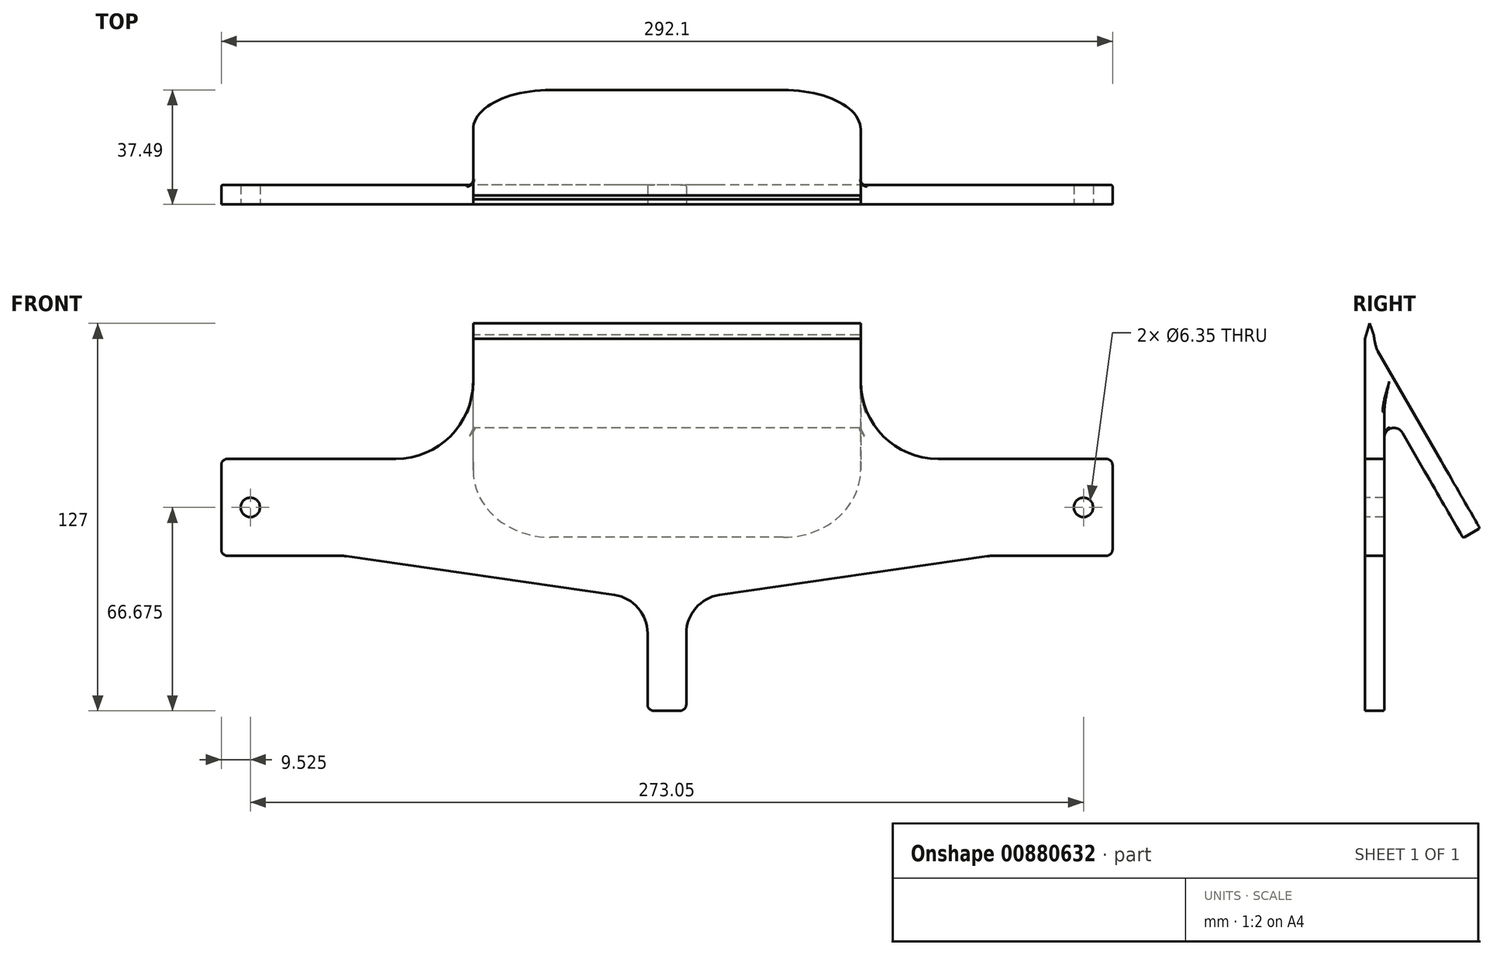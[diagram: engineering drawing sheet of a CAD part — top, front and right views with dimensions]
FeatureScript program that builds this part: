
annotation { "Feature Type Name" : "Feature", "Feature Type Description" : "" }
export const myFeature = defineFeature(function(context is Context, id is Id, definition is map)
    precondition{}
    {
        {
            var Q0;
            Q0=qCreatedBy(makeId("Right.planeOp"),FACE);
            var sketch = newSketch(context, id + "F0", { "sketchPlane" : qUnion([Q0])});
            skLineSegment(sketch, "E0", {"start": v(4.75, -127) * mm, "end": v(-1.6, -127) * mm});
            skLineSegment(sketch, "E1", {"start": v(-1.6, -127) * mm, "end": v(-1.6, -5.08) * mm});
            skPoint(sketch, "E2.orphan", {"position": v(-1.6, 0) * mm});
            skPoint(sketch, "E3.orphan", {"position": v(1.6, 0) * mm});
            skArc(sketch, "E4", {"start": v(1.27, -3.8) * mm, "mid": v(1.68, -6.21) * mm, "end": v(2.33, -8.56) * mm});
            skPoint(sketch, "E5.orphan", {"position": v(5.41, -5.08) * mm});
            skLineSegment(sketch, "E6", {"start": v(2.6, -9.17) * mm, "end": v(36.08, -67.16) * mm});
            skLineSegment(sketch, "E7", {"start": v(36.08, -67.16) * mm, "end": v(30.58, -70.33) * mm});
            skLineSegment(sketch, "E8", {"start": v(30.58, -70.33) * mm, "end": v(10.67, -35.86) * mm});
            skLineSegment(sketch, "E9", {"start": v(4.75, -127) * mm, "end": v(4.75, -37.45) * mm});
            skPoint(sketch, "E10.visualSharp", {"position": v(4.75, -25.6) * mm});
            skArc(sketch, "E10.filletArc", {"start": v(10.67, -35.86) * mm, "mid": v(7.1, -34.38) * mm, "end": v(4.75, -37.45) * mm});
            skPoint(sketch, "E11.visualSharp", {"position": v(2.44, -8.89) * mm});
            skArc(sketch, "E11.filletArc", {"start": v(2.33, -8.56) * mm, "mid": v(2.45, -8.87) * mm, "end": v(2.6, -9.17) * mm});
            skLineSegment(sketch, "E12", {"start": v(0, 0) * mm, "end": v(1.27, -3.8) * mm});
            skLineSegment(sketch, "E13", {"start": v(0, 0) * mm, "end": v(-1.6, -5.08) * mm});
            skSolve(sketch);
        }
        {
            var Q0;
            Q0=qSketchRegion(id+"F0",true);
            extrude(context, id + "F1", {"entities" : qUnion([Q0]), "endBound" : BoundingType.SYMMETRIC, "offsetDistance" : 25.4 * mm, "depth" : 292.1 * mm});
        }
        {
            var Q0;
            Q0=makeQuery(id+"F1.opExtrude","SWEPT_FACE",FACE,{"disambiguationData":[OSD([sQuery(id+"F0.wireOp",EDGE,"E1")])]});
            var sketch = newSketch(context, id + "F2", { "sketchPlane" : qUnion([Q0])});
            skLineSegment(sketch, "E14", {"start": v(-63.5, 0) * mm, "end": v(-63.5, -19.05) * mm});
            skLineSegment(sketch, "E15", {"start": v(-88.9, -44.45) * mm, "end": v(-144.02, -44.45) * mm});
            skLineSegment(sketch, "E16", {"start": v(-146.05, -46.48) * mm, "end": v(-146.05, -74.17) * mm});
            skLineSegment(sketch, "E17", {"start": v(-144.02, -76.2) * mm, "end": v(-106.83, -76.2) * mm});
            skLineSegment(sketch, "E18", {"start": v(-6.35, -101.6) * mm, "end": v(-6.35, -124.97) * mm});
            skLineSegment(sketch, "E19", {"start": v(-4.32, -127) * mm, "end": v(4.32, -127) * mm});
            skLineSegment(sketch, "E20", {"start": v(6.35, -124.97) * mm, "end": v(6.35, -101.6) * mm});
            skLineSegment(sketch, "E21", {"start": v(106.83, -76.2) * mm, "end": v(144.02, -76.2) * mm});
            skLineSegment(sketch, "E22", {"start": v(146.05, -74.17) * mm, "end": v(146.05, -46.48) * mm});
            skLineSegment(sketch, "E23", {"start": v(144.02, -44.45) * mm, "end": v(88.9, -44.45) * mm});
            skLineSegment(sketch, "E24", {"start": v(63.5, -19.05) * mm, "end": v(63.5, 0) * mm});
            skLineSegment(sketch, "E25", {"start": v(63.5, 0) * mm, "end": v(-63.5, 0) * mm});
            skLineSegment(sketch, "E26", {"start": v(0, 0) * mm, "end": v(0, -127) * mm, "construction": true});
            skPoint(sketch, "E27.visualSharp", {"position": v(-6.35, -76.2) * mm});
            skPoint(sketch, "E28.visualSharp", {"position": v(6.35, -76.2) * mm});
            skPoint(sketch, "E29.visualSharp", {"position": v(-63.5, -44.45) * mm});
            skArc(sketch, "E29.filletArc", {"start": v(-88.9, -44.45) * mm, "mid": v(-70.94, -37.01) * mm, "end": v(-63.5, -19.05) * mm});
            skPoint(sketch, "E30.visualSharp", {"position": v(6.35, -127) * mm});
            skArc(sketch, "E30.filletArc", {"start": v(4.32, -127) * mm, "mid": v(5.75, -126.4) * mm, "end": v(6.35, -124.97) * mm});
            skPoint(sketch, "E31.visualSharp", {"position": v(-6.35, -127) * mm});
            skArc(sketch, "E31.filletArc", {"start": v(-6.35, -124.97) * mm, "mid": v(-5.75, -126.4) * mm, "end": v(-4.32, -127) * mm});
            skPoint(sketch, "E32.visualSharp", {"position": v(146.05, -76.2) * mm});
            skArc(sketch, "E32.filletArc", {"start": v(144.02, -76.2) * mm, "mid": v(145.45, -75.6) * mm, "end": v(146.05, -74.17) * mm});
            skPoint(sketch, "E33.visualSharp", {"position": v(146.05, -44.45) * mm});
            skArc(sketch, "E33.filletArc", {"start": v(146.05, -46.48) * mm, "mid": v(145.45, -45.05) * mm, "end": v(144.02, -44.45) * mm});
            skPoint(sketch, "E34.visualSharp", {"position": v(63.5, -44.45) * mm});
            skArc(sketch, "E34.filletArc", {"start": v(63.5, -19.05) * mm, "mid": v(70.94, -37.01) * mm, "end": v(88.9, -44.45) * mm});
            skPoint(sketch, "E35.visualSharp", {"position": v(-146.05, -76.2) * mm});
            skArc(sketch, "E35.filletArc", {"start": v(-146.05, -74.17) * mm, "mid": v(-145.45, -75.6) * mm, "end": v(-144.02, -76.2) * mm});
            skPoint(sketch, "E36.visualSharp", {"position": v(-146.05, -44.45) * mm});
            skArc(sketch, "E36.filletArc", {"start": v(-144.02, -44.45) * mm, "mid": v(-145.45, -45.05) * mm, "end": v(-146.05, -46.48) * mm});
            skCircle(sketch, "E37", {"center": v(-136.53, -60.33) * mm, "radius": 3.18 * mm});
            skCircle(sketch, "E38", {"center": v(136.53, -60.32) * mm, "radius": 3.18 * mm});
            skLineSegment(sketch, "E39", {"start": v(-146.05, -60.33) * mm, "end": v(146.05, -60.32) * mm, "construction": true});
            skLineSegment(sketch, "E40", {"start": v(-200.77, 56.14) * mm, "end": v(184.37, 56.14) * mm});
            skLineSegment(sketch, "E41", {"start": v(184.37, 56.14) * mm, "end": v(184.37, -324.86) * mm});
            skLineSegment(sketch, "E42", {"start": v(184.37, -324.86) * mm, "end": v(-200.77, -324.86) * mm});
            skLineSegment(sketch, "E43", {"start": v(-200.77, -324.86) * mm, "end": v(-200.77, 56.14) * mm});
            skPoint(sketch, "E44.orphan", {"position": v(-200.77, 56.14) * mm});
            skLineSegment(sketch, "E45", {"start": v(105.01, -76.33) * mm, "end": v(17.23, -89.03) * mm});
            skLineSegment(sketch, "E46", {"start": v(-17.23, -89.03) * mm, "end": v(-105.01, -76.33) * mm});
            skPoint(sketch, "E47.visualSharp", {"position": v(-105.92, -76.2) * mm});
            skArc(sketch, "E47.filletArc", {"start": v(-105.01, -76.33) * mm, "mid": v(-105.92, -76.23) * mm, "end": v(-106.83, -76.2) * mm});
            skPoint(sketch, "E48.visualSharp", {"position": v(-6.35, -90.6) * mm});
            skArc(sketch, "E48.filletArc", {"start": v(-6.35, -101.6) * mm, "mid": v(-9.45, -93.29) * mm, "end": v(-17.23, -89.03) * mm});
            skPoint(sketch, "E49.visualSharp", {"position": v(6.35, -90.6) * mm});
            skArc(sketch, "E49.filletArc", {"start": v(17.23, -89.03) * mm, "mid": v(9.45, -93.29) * mm, "end": v(6.35, -101.6) * mm});
            skPoint(sketch, "E50.visualSharp", {"position": v(105.92, -76.2) * mm});
            skArc(sketch, "E50.filletArc", {"start": v(106.83, -76.2) * mm, "mid": v(105.92, -76.23) * mm, "end": v(105.01, -76.33) * mm});
            skSolve(sketch);
        }
        {
            var Q0;
            Q0=qSketchRegion(id+"F2",true);
            var Q1;
            Q1=makeQuery(id+"F2.imprint","IMPRINT",FACE,{"disambiguationData":[TD([[makeQuery(id+"F2.imprint","IMPRINT",EDGE,{"derivedFrom":sQuery(id+"F2.wireOp",EDGE,"E37")}),1.0]])]});
            var Q2;
            Q2=makeQuery(id+"F2.imprint","IMPRINT",FACE,{"disambiguationData":[TD([[makeQuery(id+"F2.imprint","IMPRINT",EDGE,{"derivedFrom":sQuery(id+"F2.wireOp",EDGE,"E38")}),1.0]])]});
            extrude(context, id + "F3", {"entities" : qUnion([Q0, Q1, Q2]), "operationType" : NewBodyOperationType.REMOVE, "oppositeDirection" : true, "depth" : 25.4 * mm});
        }
        {
            var Q0;
            Q0=qCreatedBy(makeId("Top.planeOp"),FACE);
            var sketch = newSketch(context, id + "F4", { "sketchPlane" : qUnion([Q0])});
            skLineSegment(sketch, "E51.bottom", {"start": v(-165.1, 4.75) * mm, "end": v(-65.1, 4.75) * mm});
            skLineSegment(sketch, "E51.top", {"start": v(-165.1, 42.85) * mm, "end": v(-63.5, 42.85) * mm});
            skLineSegment(sketch, "E51.left", {"start": v(-165.1, 4.75) * mm, "end": v(-165.1, 42.85) * mm});
            skLineSegment(sketch, "E51.right", {"start": v(-63.5, 6.35) * mm, "end": v(-63.5, 42.85) * mm});
            skLineSegment(sketch, "E52.bottom", {"start": v(165.1, 4.75) * mm, "end": v(65.1, 4.75) * mm});
            skLineSegment(sketch, "E52.top", {"start": v(165.1, 42.85) * mm, "end": v(63.5, 42.85) * mm});
            skLineSegment(sketch, "E52.left", {"start": v(165.1, 4.75) * mm, "end": v(165.1, 42.85) * mm});
            skLineSegment(sketch, "E52.right", {"start": v(63.5, 6.35) * mm, "end": v(63.5, 42.85) * mm});
            skPoint(sketch, "E53.visualSharp", {"position": v(63.5, 4.75) * mm});
            skArc(sketch, "E53.filletArc", {"start": v(63.5, 6.35) * mm, "mid": v(63.97, 5.22) * mm, "end": v(65.1, 4.75) * mm});
            skPoint(sketch, "E54.visualSharp", {"position": v(-63.5, 4.75) * mm});
            skArc(sketch, "E54.filletArc", {"start": v(-65.1, 4.75) * mm, "mid": v(-63.97, 5.22) * mm, "end": v(-63.5, 6.35) * mm});
            skSolve(sketch);
        }
        {
            var Q0;
            Q0 = qSketchRegion(id + "F4", true);
            extrude(context, id + "F5", {"entities" : qUnion([Q0]), "operationType" : NewBodyOperationType.REMOVE, "oppositeDirection" : true, "depth" : 135.89 * mm, "offsetDistance" : 25.4 * mm});
        }
        {
            var Q0;
            Q0=makeQuery(id+"F1.opExtrude","SWEPT_FACE",FACE,{"disambiguationData":[OSD([sQuery(id+"F0.wireOp",EDGE,"E8")])]});
            var sketch = newSketch(context, id + "F6", { "sketchPlane" : qUnion([Q0])});
            skLineSegment(sketch, "E55", {"start": v(63.5, -42.96) * mm, "end": v(63.5, -50.8) * mm});
            skLineSegment(sketch, "E56", {"start": v(38.1, -76.2) * mm, "end": v(34.26, -76.2) * mm});
            skLineSegment(sketch, "E57", {"start": v(34.26, -76.2) * mm, "end": v(34.26, -96.1) * mm});
            skLineSegment(sketch, "E58", {"start": v(34.26, -96.1) * mm, "end": v(73.35, -96.1) * mm});
            skLineSegment(sketch, "E59", {"start": v(73.35, -96.1) * mm, "end": v(73.35, -42.8) * mm});
            skLineSegment(sketch, "E60", {"start": v(73.35, -42.8) * mm, "end": v(63.5, -42.96) * mm});
            skPoint(sketch, "E61.visualSharp", {"position": v(63.5, -76.2) * mm});
            skArc(sketch, "E61.filletArc", {"start": v(38.1, -76.2) * mm, "mid": v(56.06, -68.76) * mm, "end": v(63.5, -50.8) * mm});
            skLineSegment(sketch, "E62", {"start": v(-63.5, -42.97) * mm, "end": v(-63.5, -50.8) * mm});
            skLineSegment(sketch, "E63", {"start": v(-38.1, -76.2) * mm, "end": v(-31.8, -76.2) * mm});
            skLineSegment(sketch, "E64", {"start": v(-31.8, -76.2) * mm, "end": v(-31.8, -90.8) * mm});
            skLineSegment(sketch, "E65", {"start": v(-31.8, -90.8) * mm, "end": v(-79.64, -90.8) * mm});
            skLineSegment(sketch, "E66", {"start": v(-79.64, -90.8) * mm, "end": v(-79.64, -42.81) * mm});
            skLineSegment(sketch, "E67", {"start": v(-79.64, -42.81) * mm, "end": v(-63.5, -42.97) * mm});
            skPoint(sketch, "E68.visualSharp", {"position": v(-63.5, -76.2) * mm});
            skArc(sketch, "E68.filletArc", {"start": v(-63.5, -50.8) * mm, "mid": v(-56.06, -68.76) * mm, "end": v(-38.1, -76.2) * mm});
            skSolve(sketch);
        }
        {
            var Q0;
            Q0 = qSketchRegion(id + "F6", true);
            extrude(context, id + "F7", {"entities" : qUnion([Q0]), "operationType" : NewBodyOperationType.REMOVE, "oppositeDirection" : true, "depth" : 25.4 * mm, "offsetDistance" : 25.4 * mm});
        }
        {
            var Q0;
            Q0=makeQuery(id+"F5.boolean.opBoolean","INTERSECT",EDGE,{"derivedFrom":[makeQuery(id+"F1.opExtrude","SWEPT_FACE",FACE,{"disambiguationData":[OSD([sQuery(id+"F0.wireOp",EDGE,"E6")])]}),makeQuery(id+"F5.opExtrude","SWEPT_FACE",FACE,{"disambiguationData":[OSD([sQuery(id+"F4.wireOp",EDGE,"E52.right")])]})]});
            var Q1;
            Q1=makeQuery(id+"F5.boolean.opBoolean","INTERSECT",EDGE,{"derivedFrom":[makeQuery(id+"F1.opExtrude","SWEPT_FACE",FACE,{"disambiguationData":[OSD([sQuery(id+"F0.wireOp",EDGE,"E10.filletArc")])]}),makeQuery(id+"F5.opExtrude","SWEPT_FACE",FACE,{"disambiguationData":[OSD([sQuery(id+"F4.wireOp",EDGE,"E54.filletArc")])]})]});
            var Q2;
            Q2=makeQuery(id+"F5.boolean.opBoolean","INTERSECT",EDGE,{"derivedFrom":[makeQuery(id+"F3.boolean.opBoolean","COPY",FACE,{"derivedFrom":makeQuery(id+"F3.opExtrude","SWEPT_FACE",FACE,{"disambiguationData":[OSD([sQuery(id+"F2.wireOp",EDGE,"E29.filletArc")])]})}),makeQuery(id+"F5.opExtrude","SWEPT_FACE",FACE,{"disambiguationData":[OSD([sQuery(id+"F4.wireOp",EDGE,"E51.bottom")])]})]});
            var Q3;
            Q3=makeQuery(id+"F3.boolean.opBoolean","COPY",EDGE,{"derivedFrom":makeQuery(id+"F3.opExtrude","CAP_EDGE",EDGE,{"disambiguationData":[OSD([sQuery(id+"F2.wireOp",EDGE,"E29.filletArc")])],"isStart":true})});
            fillet(context, id + "F8", {"entities" : qUnion([Q0, Q1, Q2, Q3]), "radius" : 0.5 * mm, "tangentPropagation" : true, "allowEdgeOverflow" : false});
        }
    });
